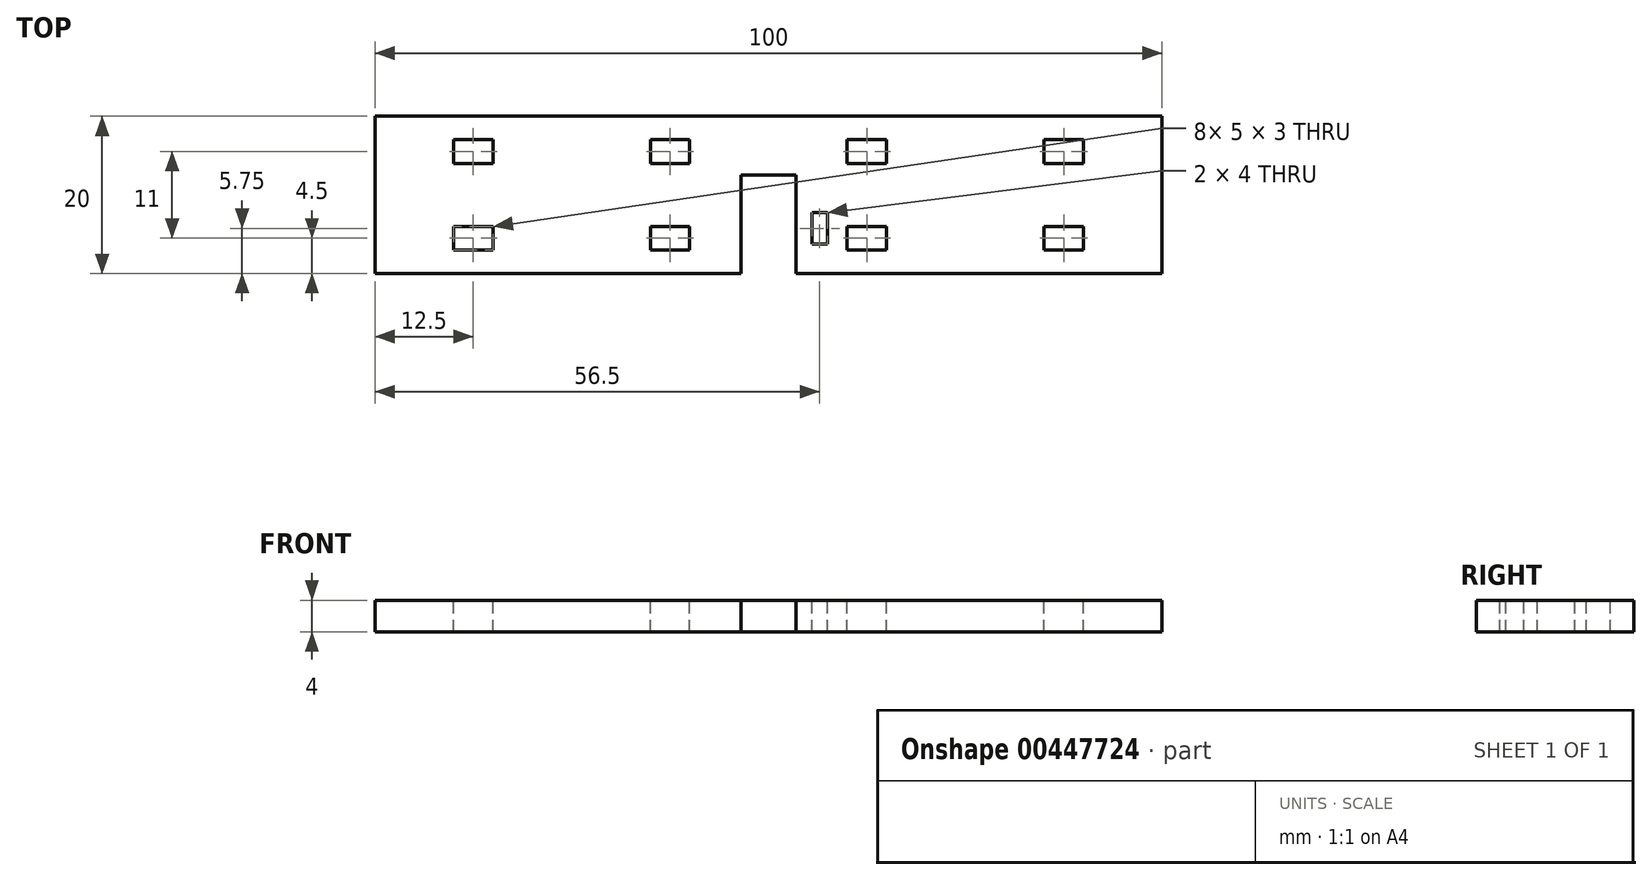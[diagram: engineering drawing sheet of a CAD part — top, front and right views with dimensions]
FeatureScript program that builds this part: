
annotation { "Feature Type Name" : "Feature", "Feature Type Description" : "" }
export const myFeature = defineFeature(function(context is Context, id is Id, definition is map)
    precondition{}
    {
        {
            var Q0;
            Q0=qCreatedBy(makeId("Top.planeOp"),FACE);
            var sketch = newSketch(context, id + "F0", { "sketchPlane" : qUnion([Q0])});
            skLineSegment(sketch, "E0.bottom", {"start": v(-50, 10) * mm, "end": v(50, 10) * mm});
            skLineSegment(sketch, "E0.top", {"start": v(-50, -10) * mm, "end": v(50, -10) * mm});
            skLineSegment(sketch, "E0.left", {"start": v(-50, 10) * mm, "end": v(-50, -10) * mm});
            skLineSegment(sketch, "E0.right", {"start": v(50, 10) * mm, "end": v(50, -10) * mm});
            skPoint(sketch, "E0.middle", {"position": v(0, 0) * mm});
            skSolve(sketch);
        }
        {
            var Q0;
            Q0 = qSketchRegion(id + "F0", true);
            extrude(context, id + "F1", {"entities" : qUnion([Q0]), "depth" : 4 * mm, "offsetDistance" : 25 * mm});
        }
        {
            var Q0;
            Q0=makeQuery(id+"F1.opExtrude","CAP_FACE",FACE,{"disambiguationData":[OSD([sQuery(id+"F0.wireOp",EDGE,"E0.bottom"),sQuery(id+"F0.wireOp",EDGE,"E0.top"),sQuery(id+"F0.wireOp",EDGE,"E0.left"),sQuery(id+"F0.wireOp",EDGE,"E0.right")])],"isStart":false});
            var sketch = newSketch(context, id + "F2", { "sketchPlane" : qUnion([Q0])});
            skLineSegment(sketch, "E1", {"start": v(-50, 0) * mm, "end": v(50, 0) * mm});
            skLineSegment(sketch, "E2", {"start": v(-50, 10) * mm, "end": v(-50, 7) * mm});
            skLineSegment(sketch, "E3", {"start": v(-50, 7) * mm, "end": v(-50, 4) * mm});
            skLineSegment(sketch, "E4", {"start": v(-50, 4) * mm, "end": v(-50, -4) * mm});
            skLineSegment(sketch, "E5", {"start": v(-50, -4) * mm, "end": v(-50, -7) * mm});
            skLineSegment(sketch, "E6", {"start": v(-50, -7) * mm, "end": v(-50, -10) * mm});
            skLineSegment(sketch, "E7", {"start": v(-50, 7) * mm, "end": v(-40, 7) * mm});
            skLineSegment(sketch, "E8.bottom", {"start": v(-40, 7) * mm, "end": v(-35, 7) * mm});
            skLineSegment(sketch, "E8.top", {"start": v(-40, 4) * mm, "end": v(-35, 4) * mm});
            skLineSegment(sketch, "E8.left", {"start": v(-40, 7) * mm, "end": v(-40, 4) * mm});
            skLineSegment(sketch, "E8.right", {"start": v(-35, 7) * mm, "end": v(-35, 4) * mm});
            skLineSegment(sketch, "E9", {"start": v(-35, 7) * mm, "end": v(-15, 7) * mm});
            skLineSegment(sketch, "E10.bottom", {"start": v(-15, 7) * mm, "end": v(-10, 7) * mm});
            skLineSegment(sketch, "E10.top", {"start": v(-15, 4) * mm, "end": v(-10, 4) * mm});
            skLineSegment(sketch, "E10.left", {"start": v(-15, 7) * mm, "end": v(-15, 4) * mm});
            skLineSegment(sketch, "E10.right", {"start": v(-10, 7) * mm, "end": v(-10, 4) * mm});
            skLineSegment(sketch, "E11", {"start": v(-10, 7) * mm, "end": v(10, 7) * mm});
            skLineSegment(sketch, "E12.bottom", {"start": v(10, 7) * mm, "end": v(15, 7) * mm});
            skLineSegment(sketch, "E12.top", {"start": v(10, 4) * mm, "end": v(15, 4) * mm});
            skLineSegment(sketch, "E12.left", {"start": v(10, 7) * mm, "end": v(10, 4) * mm});
            skLineSegment(sketch, "E12.right", {"start": v(15, 7) * mm, "end": v(15, 4) * mm});
            skLineSegment(sketch, "E13", {"start": v(15, 7) * mm, "end": v(35, 7) * mm});
            skLineSegment(sketch, "E14.bottom", {"start": v(35, 7) * mm, "end": v(40, 7) * mm});
            skLineSegment(sketch, "E14.top", {"start": v(35, 4) * mm, "end": v(40, 4) * mm});
            skLineSegment(sketch, "E14.left", {"start": v(35, 7) * mm, "end": v(35, 4) * mm});
            skLineSegment(sketch, "E14.right", {"start": v(40, 7) * mm, "end": v(40, 4) * mm});
            skLineSegment(sketch, "E15", {"start": v(40, 7) * mm, "end": v(50, 7) * mm});
            skLineSegment(sketch, "E16", {"start": v(-50, -7) * mm, "end": v(-40, -7) * mm});
            skLineSegment(sketch, "E17.bottom", {"start": v(-40, -7) * mm, "end": v(-35, -7) * mm});
            skLineSegment(sketch, "E17.top", {"start": v(-40, -4) * mm, "end": v(-35, -4) * mm});
            skLineSegment(sketch, "E17.left", {"start": v(-40, -7) * mm, "end": v(-40, -4) * mm});
            skLineSegment(sketch, "E17.right", {"start": v(-35, -7) * mm, "end": v(-35, -4) * mm});
            skLineSegment(sketch, "E18", {"start": v(-35, -7) * mm, "end": v(-15, -7) * mm});
            skLineSegment(sketch, "E19.bottom", {"start": v(-15, -7) * mm, "end": v(-10, -7) * mm});
            skLineSegment(sketch, "E19.top", {"start": v(-15, -4) * mm, "end": v(-10, -4) * mm});
            skLineSegment(sketch, "E19.left", {"start": v(-15, -7) * mm, "end": v(-15, -4) * mm});
            skLineSegment(sketch, "E19.right", {"start": v(-10, -7) * mm, "end": v(-10, -4) * mm});
            skLineSegment(sketch, "E20", {"start": v(-10, -7) * mm, "end": v(10, -7) * mm});
            skLineSegment(sketch, "E21.bottom", {"start": v(10, -7) * mm, "end": v(15, -7) * mm});
            skLineSegment(sketch, "E21.top", {"start": v(10, -4) * mm, "end": v(15, -4) * mm});
            skLineSegment(sketch, "E21.left", {"start": v(10, -7) * mm, "end": v(10, -4) * mm});
            skLineSegment(sketch, "E21.right", {"start": v(15, -7) * mm, "end": v(15, -4) * mm});
            skLineSegment(sketch, "E22", {"start": v(15, -7) * mm, "end": v(35, -7) * mm});
            skLineSegment(sketch, "E23.bottom", {"start": v(35, -7) * mm, "end": v(40, -7) * mm});
            skLineSegment(sketch, "E23.top", {"start": v(35, -4) * mm, "end": v(40, -4) * mm});
            skLineSegment(sketch, "E23.left", {"start": v(35, -7) * mm, "end": v(35, -4) * mm});
            skLineSegment(sketch, "E23.right", {"start": v(40, -7) * mm, "end": v(40, -4) * mm});
            skLineSegment(sketch, "E24", {"start": v(40, -7) * mm, "end": v(50, -7) * mm});
            skLineSegment(sketch, "E25.bottom", {"start": v(-3.5, 2.5) * mm, "end": v(3.5, 2.5) * mm});
            skLineSegment(sketch, "E25.top", {"start": v(-3.5, -2.5) * mm, "end": v(3.5, -2.5) * mm});
            skLineSegment(sketch, "E25.left", {"start": v(-3.5, 2.5) * mm, "end": v(-3.5, -2.5) * mm});
            skLineSegment(sketch, "E25.right", {"start": v(3.5, 2.5) * mm, "end": v(3.5, -2.5) * mm});
            skPoint(sketch, "E25.middle", {"position": v(0, 0) * mm});
            skLineSegment(sketch, "E26", {"start": v(-3.5, -2.5) * mm, "end": v(-3.5, -10) * mm});
            skLineSegment(sketch, "E27", {"start": v(3.5, -2.5) * mm, "end": v(3.5, -10) * mm});
            skLineSegment(sketch, "E28", {"start": v(-3.5, -10) * mm, "end": v(-5.5, -10) * mm});
            skLineSegment(sketch, "E29", {"start": v(-5.5, -10) * mm, "end": v(-5.5, -2.25) * mm});
            skLineSegment(sketch, "E30", {"start": v(-5.5, -2.25) * mm, "end": v(-7.5, -2.25) * mm});
            skLineSegment(sketch, "E31", {"start": v(-7.5, -2.25) * mm, "end": v(-7.5, -10) * mm});
            skLineSegment(sketch, "E32.bottom", {"start": v(-7.5, -2.25) * mm, "end": v(-5.5, -2.25) * mm});
            skLineSegment(sketch, "E32.top", {"start": v(-7.5, -6.25) * mm, "end": v(-5.5, -6.25) * mm});
            skLineSegment(sketch, "E32.left", {"start": v(-7.5, -2.25) * mm, "end": v(-7.5, -6.25) * mm});
            skLineSegment(sketch, "E32.right", {"start": v(-5.5, -2.25) * mm, "end": v(-5.5, -6.25) * mm});
            skLineSegment(sketch, "E33", {"start": v(3.5, -10) * mm, "end": v(5.5, -10) * mm});
            skLineSegment(sketch, "E34", {"start": v(5.5, -10) * mm, "end": v(5.5, -2.25) * mm});
            skLineSegment(sketch, "E35", {"start": v(5.5, -2.25) * mm, "end": v(7.5, -2.25) * mm});
            skLineSegment(sketch, "E36", {"start": v(7.5, -2.25) * mm, "end": v(7.5, -10.25) * mm});
            skLineSegment(sketch, "E37.top", {"start": v(5.5, -6.25) * mm, "end": v(7.5, -6.25) * mm});
            skLineSegment(sketch, "E37.left", {"start": v(5.5, -2.25) * mm, "end": v(5.5, -6.25) * mm});
            skLineSegment(sketch, "E37.right", {"start": v(7.5, -2.25) * mm, "end": v(7.5, -6.25) * mm});
            skSolve(sketch);
        }
        {
            var Q0;
            Q0=makeQuery(id+"F2.imprint","IMPRINT",FACE,{"disambiguationData":[TD([[makeQuery(id+"F2.imprint","IMPRINT",EDGE,{"derivedFrom":sQuery(id+"F2.wireOp",EDGE,"E8.bottom")}),-1.0]])]});
            var Q1;
            Q1=makeQuery(id+"F2.imprint","IMPRINT",FACE,{"disambiguationData":[TD([[makeQuery(id+"F2.imprint","IMPRINT",EDGE,{"derivedFrom":sQuery(id+"F2.wireOp",EDGE,"E17.bottom")}),1.0]])]});
            var Q2;
            Q2=makeQuery(id+"F2.imprint","IMPRINT",FACE,{"disambiguationData":[TD([[makeQuery(id+"F2.imprint","IMPRINT",EDGE,{"derivedFrom":sQuery(id+"F2.wireOp",EDGE,"E19.bottom")}),1.0]])]});
            var Q3;
            Q3=makeQuery(id+"F2.imprint","IMPRINT",FACE,{"disambiguationData":[TD([[makeQuery(id+"F2.imprint","IMPRINT",EDGE,{"derivedFrom":sQuery(id+"F2.wireOp",EDGE,"E10.bottom")}),-1.0]])]});
            var Q4;
            {var subQ5=sQuery(id+"F2.wireOp",EDGE,"E25.bottom");Q4=makeQuery(id+"F2.imprint","IMPRINT",FACE,{"disambiguationData":[TD([[makeQuery(id+"F2.imprint","IMPRINT",EDGE,{"derivedFrom":subQ5}),-1.0]])]});}
            var Q5;
            {var subQ5=sQuery(id+"F2.wireOp",EDGE,"E25.top");Q5=makeQuery(id+"F2.imprint","IMPRINT",FACE,{"disambiguationData":[TD([[makeQuery(id+"F2.imprint","IMPRINT",EDGE,{"derivedFrom":subQ5}),1.0]])]});}
            var Q6;
            Q6=makeQuery(id+"F2.imprint","IMPRINT",FACE,{"disambiguationData":[TD([[makeQuery(id+"F2.imprint","IMPRINT",EDGE,{"derivedFrom":sQuery(id+"F2.wireOp",EDGE,"E32.bottom")}),-1.0]])]});
            var Q7;
            Q7=makeQuery(id+"F2.imprint","IMPRINT",FACE,{"disambiguationData":[TD([[makeQuery(id+"F2.imprint","IMPRINT",EDGE,{"derivedFrom":sQuery(id+"F2.wireOp",EDGE,"E35")}),-1.0]])]});
            var Q8;
            Q8=makeQuery(id+"F2.imprint","IMPRINT",FACE,{"disambiguationData":[TD([[makeQuery(id+"F2.imprint","IMPRINT",EDGE,{"derivedFrom":sQuery(id+"F2.wireOp",EDGE,"E21.bottom")}),1.0]])]});
            var Q9;
            Q9=makeQuery(id+"F2.imprint","IMPRINT",FACE,{"disambiguationData":[TD([[makeQuery(id+"F2.imprint","IMPRINT",EDGE,{"derivedFrom":sQuery(id+"F2.wireOp",EDGE,"E12.bottom")}),-1.0]])]});
            var Q10;
            Q10=makeQuery(id+"F2.imprint","IMPRINT",FACE,{"disambiguationData":[TD([[makeQuery(id+"F2.imprint","IMPRINT",EDGE,{"derivedFrom":sQuery(id+"F2.wireOp",EDGE,"E14.bottom")}),-1.0]])]});
            var Q11;
            Q11=makeQuery(id+"F2.imprint","IMPRINT",FACE,{"disambiguationData":[TD([[makeQuery(id+"F2.imprint","IMPRINT",EDGE,{"derivedFrom":sQuery(id+"F2.wireOp",EDGE,"E23.bottom")}),1.0]])]});
            var Q12;
            {var subQ5=sQuery(id+"F2.wireOp",EDGE,"E25.top");Q12=makeQuery(id+"F2.imprint","IMPRINT",FACE,{"disambiguationData":[TD([[makeQuery(id+"F2.imprint","IMPRINT",EDGE,{"derivedFrom":subQ5}),-1.0]])]});}
            var Q13;
            {var subQ0=sQuery(id+"F2.wireOp",EDGE,"E26");var subQ1=sQuery(id+"F2.wireOp",EDGE,"E20");var subQ2=makeQuery(id+"F2.imprint","INTERSECT",VERTEX,{"derivedFrom":[subQ1,subQ0]});Q13=makeQuery(id+"F2.imprint","IMPRINT",FACE,{"disambiguationData":[TD([[makeQuery(id+"F2.imprint","IMPRINT",EDGE,{"disambiguationData":[TD([[subQ2,-1.0]])],"derivedFrom":subQ1}),-1.0]])]});}
            extrude(context, id + "F3", {"entities" : qUnion([Q0, Q1, Q2, Q3, Q4, Q5, Q6, Q7, Q8, Q9, Q10, Q11, Q12, Q13]), "operationType" : NewBodyOperationType.REMOVE, "oppositeDirection" : true, "depth" : 4 * mm, "offsetDistance" : 25 * mm});
        }
    });
